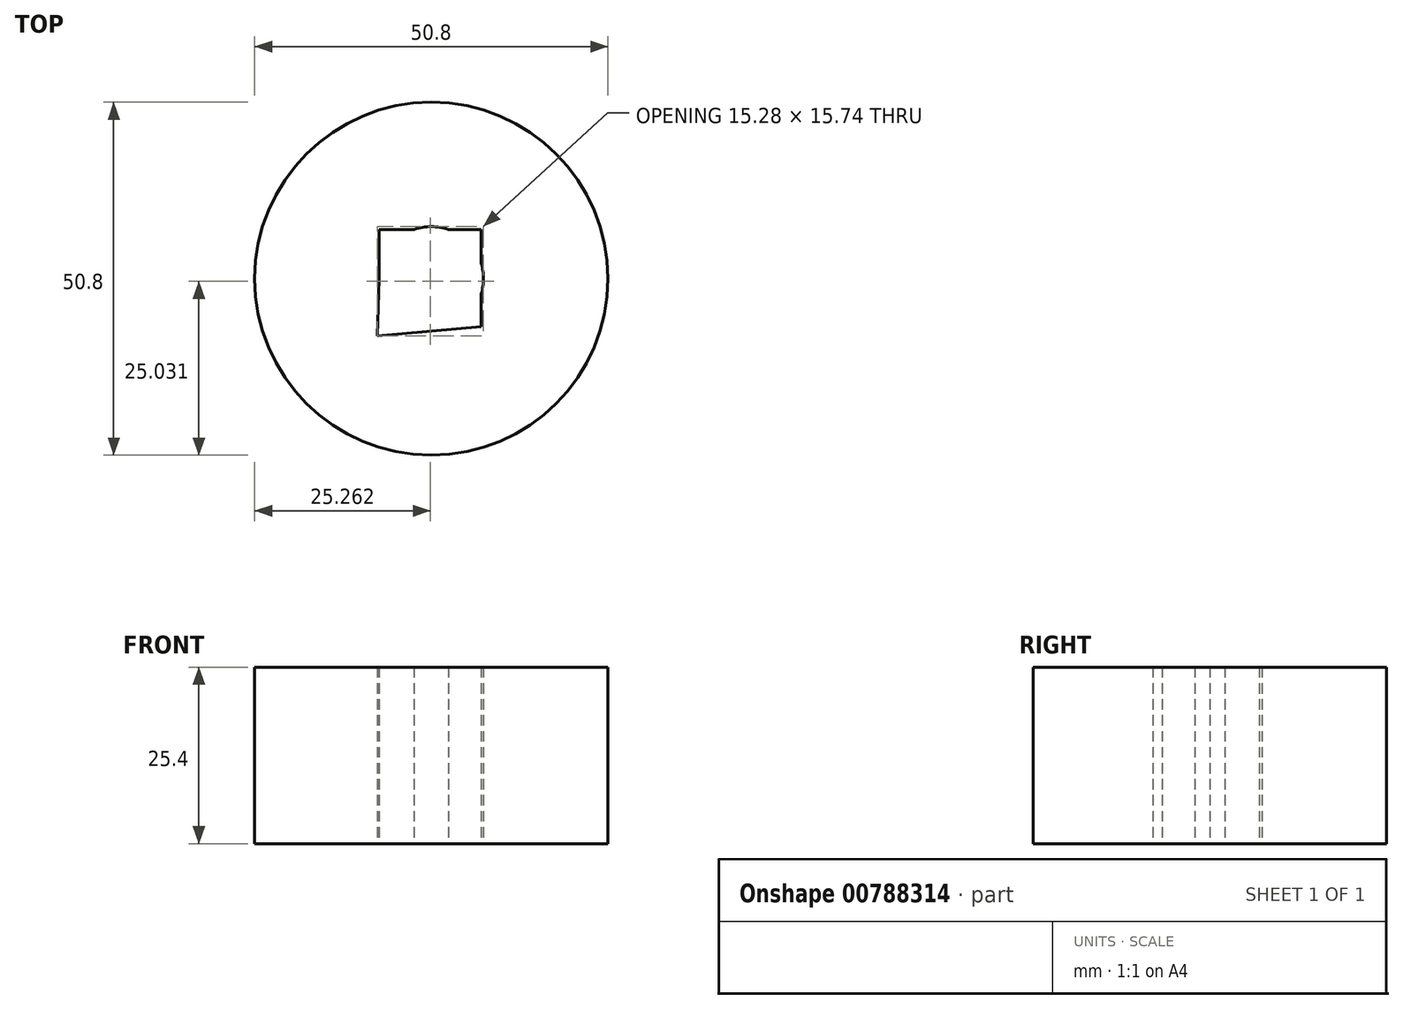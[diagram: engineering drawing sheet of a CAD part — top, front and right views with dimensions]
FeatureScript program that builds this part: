
annotation { "Feature Type Name" : "Feature", "Feature Type Description" : "" }
export const myFeature = defineFeature(function(context is Context, id is Id, definition is map)
    precondition{}
    {
        {
            var Q0;
            Q0=qCreatedBy(makeId("Top.planeOp"),FACE);
            var sketch = newSketch(context, id + "F0", { "sketchPlane" : qUnion([Q0])});
            skCircle(sketch, "E0", {"center": v(0, 0) * mm, "radius": 7.5 * mm});
            skCircle(sketch, "E1", {"center": v(0, 0) * mm, "radius": 25.4 * mm});
            skLineSegment(sketch, "E2", {"start": v(-7.5, 0) * mm, "end": v(-7.5, 7.08) * mm});
            skLineSegment(sketch, "E3", {"start": v(-7.5, 7.08) * mm, "end": v(7.18, 7.08) * mm});
            skLineSegment(sketch, "E4", {"start": v(7.18, 7.08) * mm, "end": v(7.18, -6.88) * mm});
            skLineSegment(sketch, "E5", {"start": v(7.18, -6.88) * mm, "end": v(-7.78, -8.24) * mm});
            skLineSegment(sketch, "E6", {"start": v(-7.78, -8.24) * mm, "end": v(-7.5, 0) * mm});
            skSolve(sketch);
        }
        {
            var Q0;
            Q0 = qSketchRegion(id + "F0", true);
            extrude(context, id + "F1", {"entities" : qUnion([Q0]), "depth" : 25.4 * mm, "offsetDistance" : 25.4 * mm});
        }
    });
